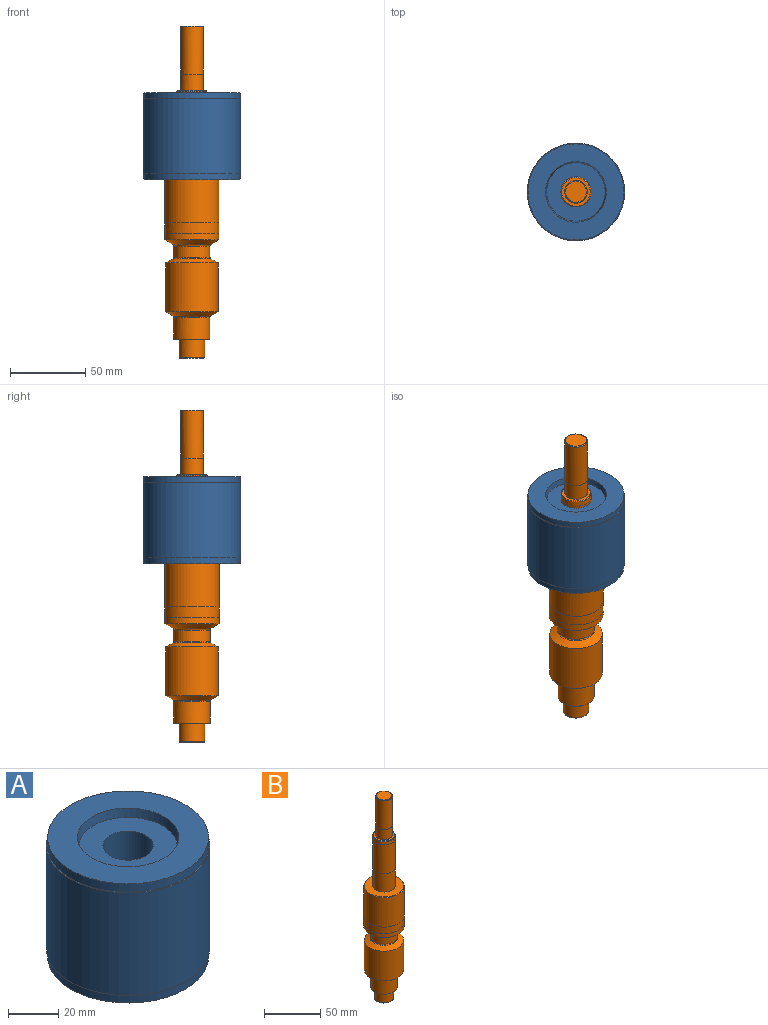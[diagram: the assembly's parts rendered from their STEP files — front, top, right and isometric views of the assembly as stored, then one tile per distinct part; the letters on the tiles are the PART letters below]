
ASSEMBLY  parts=2 mates=1
PART A: 12 faces, bbox 65x65x58 mm
  f0: plane 39x39mm, normal (0,0,-1), area 880.4mm2, adj f1,f11
  f1: cone r=20.21mm half-angle=10deg, axis (0,0,-1), area 506.6mm2, adj f0,f2
  f2: plane 64x64mm, normal (0,0,-1), area 1934.4mm2, adj f1,f3
  f3: cone r=32.07mm half-angle=1deg, axis (0,0,1), area 805.2mm2, adj f2,f4
  f4: plane 65x65mm, normal (0,0,-1), area 87.3mm2, adj f3,f5
  f5: cylinder r=32.5mm len=65mm, axis (0,0,1), area 10210.2mm2, adj f4,f6
  f6: plane 65x65mm, normal (0,0,1), area 87.3mm2, adj f5,f7
  f7: cone r=32mm half-angle=1deg, axis (0,0,-1), area 805.2mm2, adj f6,f8
  f8: plane 64x64mm, normal (0,0,1), area 1934.4mm2, adj f7,f9
  f9: cone r=20.21mm half-angle=10deg, axis (0,0,1), area 506.6mm2, adj f8,f10
  f10: plane 39x39mm, normal (0,0,1), area 880.4mm2, adj f9,f11
  f11: cylinder r=10mm len=50mm, axis (0,0,1), area 3141.6mm2, adj f0,f10
PART B: 28 faces, bbox 36x36x221.2 mm
  f0: cylinder r=18mm len=36mm, axis (0,0,1), area 791.7mm2, adj f1,f16
  f1: cylinder r=18mm len=36mm, axis (0,0,1), area 492.9mm2, adj f0,f15
  f2: cylinder r=10mm len=20mm, axis (0,0,1), area 219.9mm2, adj f4,f26
  f3: cylinder r=7.5mm len=31.5mm, axis (0,0,1), area 1484.4mm2, adj f20,f27
  f4: cylinder r=10mm len=31.5mm, axis (0,0,1), area 1979.2mm2, adj f2,f18
  f5: cylinder r=8.5mm len=17mm, axis (0,0,1), area 614.2mm2, adj f6,f24
  f6: plane 23x23mm, normal (0,0,-1), area 188.5mm2, adj f5,f25
  f7: cylinder r=12mm len=24mm, axis (0,0,1), area 1100.8mm2, adj f8,f25
  f8: torus R=13mm, axis (0,0,1), area 80.1mm2, adj f7,f9
  f9: cone r=12.5mm half-angle=60deg, axis (0,0,1), area 544.1mm2, adj f8,f10
  f10: cylinder r=17.5mm len=35mm, axis (0,0,1), area 3573mm2, adj f9,f11
  f11: cone r=17.5mm half-angle=60deg, axis (0,0,-1), area 544.1mm2, adj f10,f12
  f12: torus R=13mm, axis (0,0,1), area 80.1mm2, adj f11,f13
  f13: cylinder r=12mm len=24mm, axis (0,0,1), area 565.5mm2, adj f12,f14
  f14: torus R=13mm, axis (0,0,1), area 80.1mm2, adj f13,f15
  f15: cone r=12.5mm half-angle=60deg, axis (0,0,1), area 608.5mm2, adj f1,f14
  f16: cylinder r=18mm len=36mm, axis (0,0,1), area 3641.7mm2, adj f0,f23
  f17: plane 35x35mm, normal (0,0,1), area 648mm2, adj f18,f23
  f18: cylinder r=10mm len=20mm, axis (0,0,1), area 1256.6mm2, adj f4,f17
  f19: plane 19x19mm, normal (0,0,1), area 106.8mm2, adj f20,f26
  f20: cylinder r=7.5mm len=15mm, axis (0,0,1), area 518.4mm2, adj f3,f19
  f21: plane 14x14mm, normal (0,0,1), area 153.9mm2, adj f27
  f22: plane 16x16mm, normal (0,0,-1), area 201.1mm2, adj f24
  f23: cone r=17.5mm half-angle=45deg, axis (0,0,-1), area 78.9mm2, adj f16,f17
  f24: cone r=8.5mm half-angle=45deg, axis (0,0,1), area 36.7mm2, adj f5,f22
  f25: cone r=12mm half-angle=45deg, axis (0,0,1), area 52.2mm2, adj f6,f7
  f26: cone r=9.5mm half-angle=45deg, axis (0,0,-1), area 43.3mm2, adj f2,f19
  f27: cone r=7mm half-angle=45deg, axis (0,0,-1), area 32.2mm2, adj f3,f21
PLACE A at identity
PLACE B at identity fixed
MATE revolute A.f3 <-> B.f26  axis (0,0,-1) through (0,0,19.18)mm
